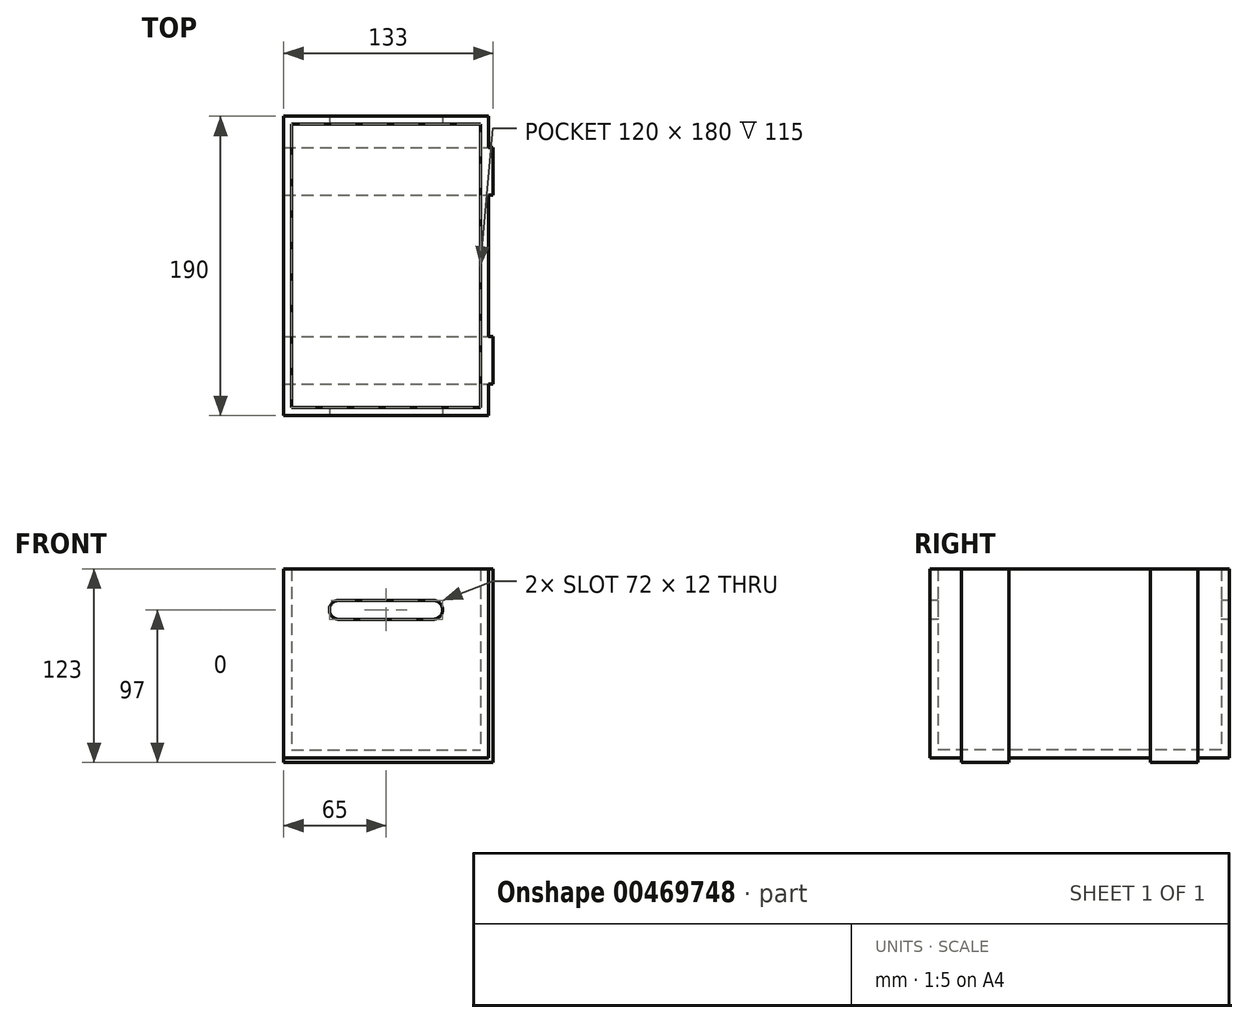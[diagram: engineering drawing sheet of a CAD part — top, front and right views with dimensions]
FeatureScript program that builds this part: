
annotation { "Feature Type Name" : "Feature", "Feature Type Description" : "" }
export const myFeature = defineFeature(function(context is Context, id is Id, definition is map)
    precondition{}
    {
        {
            var Q0;
            Q0=qCreatedBy(makeId("Top.planeOp"),FACE);
            var sketch = newSketch(context, id + "F0", { "sketchPlane" : qUnion([Q0])});
            skLineSegment(sketch, "E0.bottom", {"start": v(-60, 90) * mm, "end": v(60, 90) * mm, "construction": true});
            skLineSegment(sketch, "E0.top", {"start": v(-60, -90) * mm, "end": v(60, -90) * mm, "construction": true});
            skLineSegment(sketch, "E0.left", {"start": v(-60, 90) * mm, "end": v(-60, -90) * mm, "construction": true});
            skLineSegment(sketch, "E0.right", {"start": v(60, 90) * mm, "end": v(60, -90) * mm, "construction": true});
            skLineSegment(sketch, "E1", {"start": v(-60, 90) * mm, "end": v(60, -90) * mm, "construction": true});
            skCircle(sketch, "E2", {"center": v(-30, -60) * mm, "radius": 30 * mm, "construction": true});
            skCircle(sketch, "E3.0.1.0", {"center": v(-30, 0) * mm, "radius": 30 * mm, "construction": true});
            skCircle(sketch, "E3.0.2.0", {"center": v(-30, 60) * mm, "radius": 30 * mm, "construction": true});
            skCircle(sketch, "E3.1.0.0", {"center": v(30, -60) * mm, "radius": 30 * mm, "construction": true});
            skCircle(sketch, "E3.1.1.0", {"center": v(30, 0) * mm, "radius": 30 * mm, "construction": true});
            skCircle(sketch, "E3.1.2.0", {"center": v(30, 60) * mm, "radius": 30 * mm, "construction": true});
            skLineSegment(sketch, "E3.direction1", {"start": v(-30, -60) * mm, "end": v(30, -60) * mm, "construction": true});
            skLineSegment(sketch, "E3.direction2", {"start": v(-30, -60) * mm, "end": v(-30, 0) * mm, "construction": true});
            skLineSegment(sketch, "E4.0", {"start": v(-65, 95) * mm, "end": v(-65, -95) * mm});
            skLineSegment(sketch, "E4.1", {"start": v(-65, 95) * mm, "end": v(65, 95) * mm});
            skLineSegment(sketch, "E4.2", {"start": v(65, 95) * mm, "end": v(65, -95) * mm});
            skLineSegment(sketch, "E4.3", {"start": v(-65, -95) * mm, "end": v(65, -95) * mm});
            skSolve(sketch);
        }
        {
            var Q0;
            Q0=qCreatedBy(makeId("Top.planeOp"),FACE);
            cPlane(context, id + "F1", {"entities" : qUnion([Q0]), "cplaneType" : CPlaneType.OFFSET, "offset" : 120 * mm, "width" : 150 * mm, "height" : 150 * mm});
        }
        {
            var Q0;
            Q0 = qSketchRegion(id + "F0", true);
            var Q1;
            Q1=qCreatedBy(id+"F1.planeOp",FACE);
            extrude(context, id + "F2", {"entities" : qUnion([Q0]), "endBound" : BoundingType.UP_TO_SURFACE, "endBoundEntityFace" : qUnion([Q1]), "depth" : 25 * mm});
        }
        {
            var Q0;
            Q0=makeQuery(id+"F2.opExtrude","CAP_FACE",FACE,{"disambiguationData":[OSD([sQuery(id+"F0.wireOp",EDGE,"E4.0"),sQuery(id+"F0.wireOp",EDGE,"E4.1"),sQuery(id+"F0.wireOp",EDGE,"E4.2"),sQuery(id+"F0.wireOp",EDGE,"E4.3")])],"isStart":false});
            shell(context, id + "F3", {"entities" : qUnion([Q0]), "thickness" : 5 * mm});
        }
        {
            var Q0;
            Q0=qCreatedBy(makeId("Front.planeOp"),FACE);
            var sketch = newSketch(context, id + "F4", { "sketchPlane" : qUnion([Q0])});
            skArc(sketch, "E5", {"start": v(-30, 100) * mm, "mid": v(-36, 94) * mm, "end": v(-30, 88) * mm});
            skArc(sketch, "E6", {"start": v(30, 88) * mm, "mid": v(36, 94) * mm, "end": v(30, 100) * mm});
            skLineSegment(sketch, "E7", {"start": v(-30, 100) * mm, "end": v(30, 100) * mm});
            skLineSegment(sketch, "E8", {"start": v(-30, 88) * mm, "end": v(30, 88) * mm});
            skLineSegment(sketch, "E9", {"start": v(0, 100) * mm, "end": v(0, 120) * mm, "construction": true});
            skPoint(sketch, "E9.endSnap0", {"position": v(0, 100) * mm});
            skSolve(sketch);
        }
        {
            var Q0;
            Q0 = qSketchRegion(id + "F4", true);
            extrude(context, id + "F5", {"entities" : qUnion([Q0]), "operationType" : NewBodyOperationType.REMOVE, "endBound" : BoundingType.THROUGH_ALL, "oppositeDirection" : true, "depth" : 25 * mm, "hasSecondDirection" : true, "secondDirectionBound" : SecondDirectionBoundingType.THROUGH_ALL, "secondDirectionOppositeDirection" : false, "secondDirectionDepth" : 25 * mm});
        }
        {
            var Q0;
            Q0=makeQuery(id+"F2.opExtrude","CAP_FACE",FACE,{"disambiguationData":[OSD([sQuery(id+"F0.wireOp",EDGE,"E4.0"),sQuery(id+"F0.wireOp",EDGE,"E4.1"),sQuery(id+"F0.wireOp",EDGE,"E4.2"),sQuery(id+"F0.wireOp",EDGE,"E4.3")])],"isStart":true});
            var sketch = newSketch(context, id + "F6", { "sketchPlane" : qUnion([Q0])});
            skLineSegment(sketch, "E10.bottom", {"start": v(-65, 45) * mm, "end": v(65, 45) * mm});
            skLineSegment(sketch, "E10.top", {"start": v(-65, 75) * mm, "end": v(65, 75) * mm});
            skLineSegment(sketch, "E10.left", {"start": v(-65, 75) * mm, "end": v(-65, 45) * mm});
            skLineSegment(sketch, "E10.right", {"start": v(65, 75) * mm, "end": v(65, 45) * mm});
            skLineSegment(sketch, "E11.bottom", {"start": v(-65, -75) * mm, "end": v(65, -75) * mm});
            skLineSegment(sketch, "E11.top", {"start": v(-65, -45) * mm, "end": v(65, -45) * mm});
            skLineSegment(sketch, "E11.left", {"start": v(-65, -45) * mm, "end": v(-65, -75) * mm});
            skLineSegment(sketch, "E11.right", {"start": v(65, -45) * mm, "end": v(65, -75) * mm});
            skLineSegment(sketch, "E12", {"start": v(0, 75) * mm, "end": v(0, -75) * mm, "construction": true});
            skSolve(sketch);
        }
        {
            var Q0;
            Q0 = qSketchRegion(id + "F6", true);
            extrude(context, id + "F7", {"entities" : qUnion([Q0]), "operationType" : NewBodyOperationType.ADD, "depth" : 3 * mm});
        }
        {
            var Q0;
            Q0=makeQuery(id+"F7.boolean.opBoolean","MERGE",FACE,{"derivedFrom":[makeQuery(id+"F2.opExtrude","SWEPT_FACE",FACE,{"disambiguationData":[OSD([sQuery(id+"F0.wireOp",EDGE,"E4.2")])]}),makeQuery(id+"F7.opExtrude","SWEPT_FACE",FACE,{"disambiguationData":[OSD([sQuery(id+"F6.wireOp",EDGE,"E10.right")])]}),makeQuery(id+"F7.opExtrude","SWEPT_FACE",FACE,{"disambiguationData":[OSD([sQuery(id+"F6.wireOp",EDGE,"E11.right")])]})]});
            var sketch = newSketch(context, id + "F8", { "sketchPlane" : qUnion([Q0])});
            skLineSegment(sketch, "E13.bottom", {"start": v(-75, -3) * mm, "end": v(-45, -3) * mm});
            skLineSegment(sketch, "E13.top", {"start": v(-75, 120) * mm, "end": v(-45, 120) * mm});
            skLineSegment(sketch, "E13.left", {"start": v(-75, -3) * mm, "end": v(-75, 120) * mm});
            skLineSegment(sketch, "E13.right", {"start": v(-45, -3) * mm, "end": v(-45, 120) * mm});
            skLineSegment(sketch, "E14.bottom", {"start": v(45, -3) * mm, "end": v(75, -3) * mm});
            skLineSegment(sketch, "E14.top", {"start": v(45, 120) * mm, "end": v(75, 120) * mm});
            skLineSegment(sketch, "E14.left", {"start": v(45, -3) * mm, "end": v(45, 120) * mm});
            skLineSegment(sketch, "E14.right", {"start": v(75, -3) * mm, "end": v(75, 120) * mm});
            skSolve(sketch);
        }
        {
            var Q0;
            Q0 = qSketchRegion(id + "F8", true);
            extrude(context, id + "F9", {"entities" : qUnion([Q0]), "operationType" : NewBodyOperationType.ADD, "depth" : 3 * mm});
        }
    });
